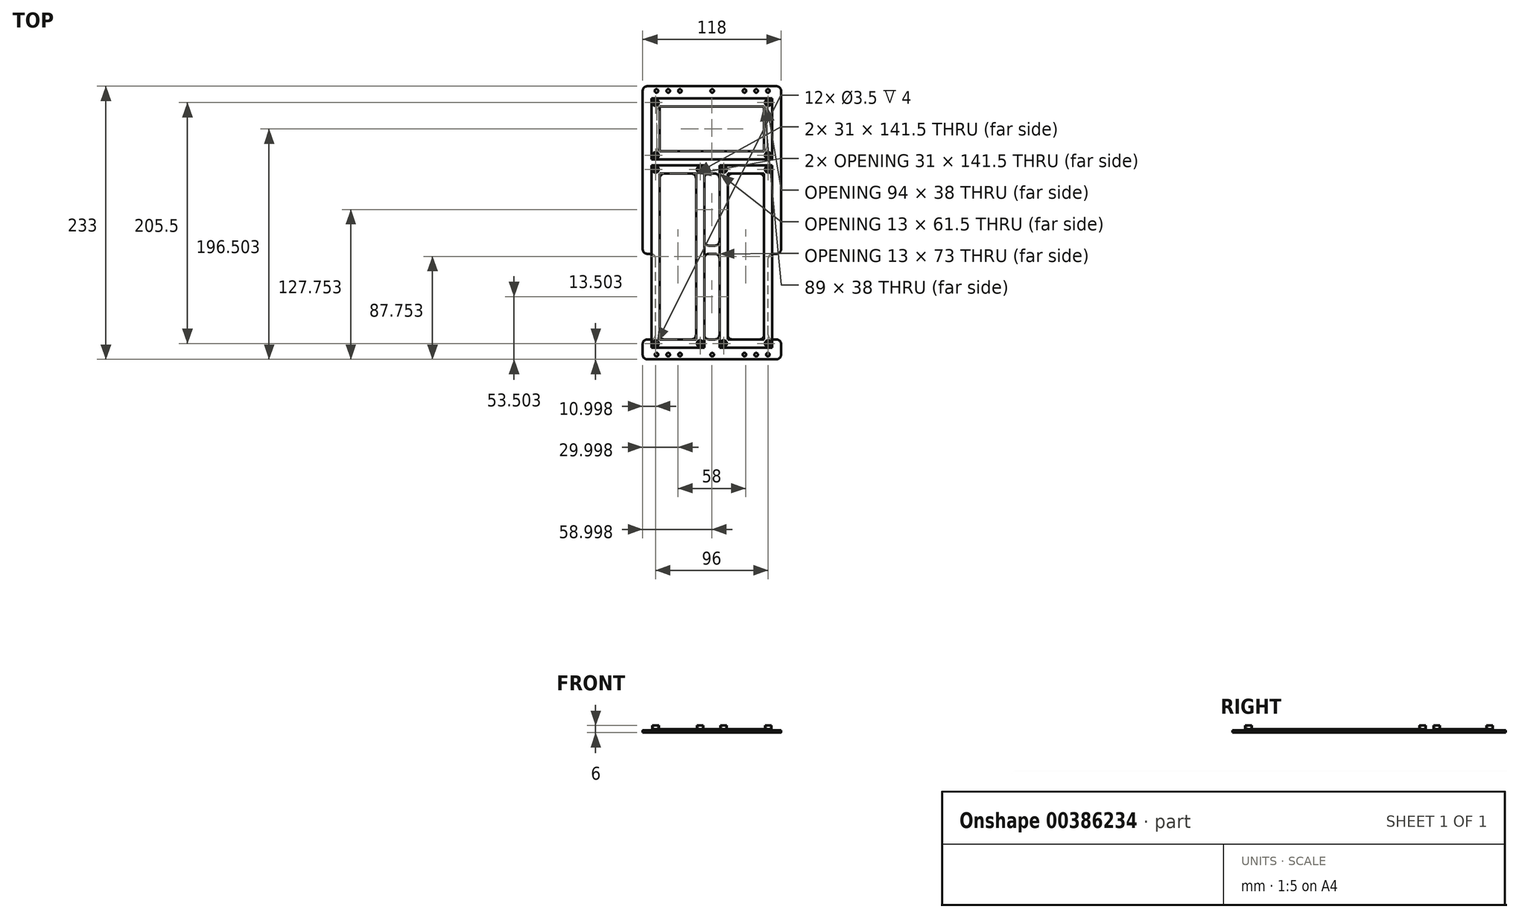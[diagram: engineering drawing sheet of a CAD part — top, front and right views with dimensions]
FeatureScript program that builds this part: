
annotation { "Feature Type Name" : "Feature", "Feature Type Description" : "" }
export const myFeature = defineFeature(function(context is Context, id is Id, definition is map)
    precondition{}
    {
        {
            var Q0;
            Q0=qCreatedBy(makeId("Top.planeOp"),FACE);
            var sketch = newSketch(context, id + "F0", { "sketchPlane" : qUnion([Q0])});
            skLineSegment(sketch, "E0.bottom", {"start": v(-51.8, 67.1) * mm, "end": v(51.2, 67.1) * mm});
            skLineSegment(sketch, "E0.top", {"start": v(-51.8, 15.1) * mm, "end": v(51.2, 15.1) * mm});
            skLineSegment(sketch, "E0.left", {"start": v(-51.8, 67.1) * mm, "end": v(-51.8, 15.1) * mm});
            skLineSegment(sketch, "E0.right", {"start": v(51.2, 67.1) * mm, "end": v(51.2, 15.1) * mm});
            skCircle(sketch, "E1", {"center": v(-48.3, 63.6) * mm, "radius": 1.75 * mm});
            skCircle(sketch, "E2", {"center": v(-48.3, 18.6) * mm, "radius": 1.75 * mm});
            skCircle(sketch, "E3", {"center": v(47.7, 18.6) * mm, "radius": 1.75 * mm});
            skCircle(sketch, "E4", {"center": v(47.7, 63.6) * mm, "radius": 1.75 * mm});
            skLineSegment(sketch, "E5.bottom", {"start": v(-44.8, 22.1) * mm, "end": v(44.2, 22.1) * mm});
            skLineSegment(sketch, "E5.top", {"start": v(-44.8, 60.1) * mm, "end": v(44.2, 60.1) * mm});
            skLineSegment(sketch, "E5.left", {"start": v(-44.8, 22.1) * mm, "end": v(-44.8, 60.1) * mm});
            skLineSegment(sketch, "E5.right", {"start": v(44.2, 22.1) * mm, "end": v(44.2, 60.1) * mm});
            skCircle(sketch, "E6", {"center": v(-48.3, 63.6) * mm, "radius": 2.75 * mm});
            skCircle(sketch, "E7", {"center": v(-48.3, 18.6) * mm, "radius": 2.75 * mm});
            skCircle(sketch, "E8", {"center": v(47.7, 18.6) * mm, "radius": 2.75 * mm});
            skCircle(sketch, "E9", {"center": v(47.7, 63.6) * mm, "radius": 2.75 * mm});
            skSolve(sketch);
        }
        {
            var Q0;
            Q0=makeQuery(id+"F0.imprint","IMPRINT",FACE,{"disambiguationData":[TD([[makeQuery(id+"F0.imprint","IMPRINT",EDGE,{"derivedFrom":sQuery(id+"F0.wireOp",EDGE,"E0.bottom")}),-1.0]])]});
            extrude(context, id + "F1", {"entities" : qUnion([Q0]), "depth" : 1 * mm});
        }
        {
            var Q0;
            Q0=makeQuery(id+"F0.imprint","IMPRINT",FACE,{"disambiguationData":[TD([[makeQuery(id+"F0.imprint","IMPRINT",EDGE,{"derivedFrom":sQuery(id+"F0.wireOp",EDGE,"E1")}),-1.0]])]});
            var Q1;
            Q1=makeQuery(id+"F0.imprint","IMPRINT",FACE,{"disambiguationData":[TD([[makeQuery(id+"F0.imprint","IMPRINT",EDGE,{"derivedFrom":sQuery(id+"F0.wireOp",EDGE,"E4")}),-1.0]])]});
            var Q2;
            Q2=makeQuery(id+"F0.imprint","IMPRINT",FACE,{"disambiguationData":[TD([[makeQuery(id+"F0.imprint","IMPRINT",EDGE,{"derivedFrom":sQuery(id+"F0.wireOp",EDGE,"E3")}),-1.0]])]});
            var Q3;
            Q3=makeQuery(id+"F0.imprint","IMPRINT",FACE,{"disambiguationData":[TD([[makeQuery(id+"F0.imprint","IMPRINT",EDGE,{"derivedFrom":sQuery(id+"F0.wireOp",EDGE,"E2")}),-1.0]])]});
            extrude(context, id + "F2", {"entities" : qUnion([Q0, Q1, Q2, Q3]), "operationType" : NewBodyOperationType.ADD, "depth" : 4 * mm});
        }
        {
            var Q0;
            Q0=qCreatedBy(makeId("Top.planeOp"),FACE);
            var sketch = newSketch(context, id + "F3", { "sketchPlane" : qUnion([Q0])});
            skLineSegment(sketch, "E10.bottom", {"start": v(-51.8, 10.1) * mm, "end": v(-6.8, 10.1) * mm});
            skLineSegment(sketch, "E10.top", {"start": v(-51.8, -145.4) * mm, "end": v(-6.8, -145.4) * mm});
            skLineSegment(sketch, "E10.left", {"start": v(-51.8, 10.1) * mm, "end": v(-51.8, -145.4) * mm});
            skLineSegment(sketch, "E10.right", {"start": v(-6.8, 10.1) * mm, "end": v(-6.8, -145.4) * mm});
            skCircle(sketch, "E11", {"center": v(-48.3, 6.6) * mm, "radius": 1.75 * mm});
            skCircle(sketch, "E12", {"center": v(-48.3, -141.9) * mm, "radius": 1.75 * mm});
            skCircle(sketch, "E13", {"center": v(-10.3, -141.9) * mm, "radius": 1.75 * mm});
            skCircle(sketch, "E14", {"center": v(-10.3, 6.6) * mm, "radius": 1.75 * mm});
            skLineSegment(sketch, "E15.bottom", {"start": v(-44.8, -138.4) * mm, "end": v(-13.8, -138.4) * mm});
            skLineSegment(sketch, "E15.top", {"start": v(-44.8, 3.1) * mm, "end": v(-13.8, 3.1) * mm});
            skLineSegment(sketch, "E15.left", {"start": v(-44.8, -138.4) * mm, "end": v(-44.8, 3.1) * mm});
            skLineSegment(sketch, "E15.right", {"start": v(-13.8, -138.4) * mm, "end": v(-13.8, 3.1) * mm});
            skCircle(sketch, "E16", {"center": v(-48.3, 6.6) * mm, "radius": 2.75 * mm});
            skCircle(sketch, "E17", {"center": v(-48.3, -141.9) * mm, "radius": 2.75 * mm});
            skCircle(sketch, "E18", {"center": v(-10.3, -141.9) * mm, "radius": 2.75 * mm});
            skCircle(sketch, "E19", {"center": v(-10.3, 6.6) * mm, "radius": 2.75 * mm});
            skSolve(sketch);
        }
        {
            var Q0;
            Q0=qCreatedBy(makeId("Top.planeOp"),FACE);
            var sketch = newSketch(context, id + "F4", { "sketchPlane" : qUnion([Q0])});
            skLineSegment(sketch, "E20.bottom", {"start": v(6.2, 10.1) * mm, "end": v(51.2, 10.1) * mm});
            skLineSegment(sketch, "E20.top", {"start": v(6.2, -145.4) * mm, "end": v(51.2, -145.4) * mm});
            skLineSegment(sketch, "E20.left", {"start": v(6.2, 10.1) * mm, "end": v(6.2, -145.4) * mm});
            skLineSegment(sketch, "E20.right", {"start": v(51.2, 10.1) * mm, "end": v(51.2, -145.4) * mm});
            skCircle(sketch, "E21", {"center": v(9.7, 6.6) * mm, "radius": 1.75 * mm});
            skCircle(sketch, "E22", {"center": v(9.7, -141.9) * mm, "radius": 1.75 * mm});
            skCircle(sketch, "E23", {"center": v(47.7, -141.9) * mm, "radius": 1.75 * mm});
            skCircle(sketch, "E24", {"center": v(47.7, 6.6) * mm, "radius": 1.75 * mm});
            skLineSegment(sketch, "E25.bottom", {"start": v(13.2, -138.4) * mm, "end": v(44.2, -138.4) * mm});
            skLineSegment(sketch, "E25.top", {"start": v(13.2, 3.1) * mm, "end": v(44.2, 3.1) * mm});
            skLineSegment(sketch, "E25.left", {"start": v(13.2, -138.4) * mm, "end": v(13.2, 3.1) * mm});
            skLineSegment(sketch, "E25.right", {"start": v(44.2, -138.4) * mm, "end": v(44.2, 3.1) * mm});
            skCircle(sketch, "E26", {"center": v(9.7, 6.6) * mm, "radius": 2.75 * mm});
            skCircle(sketch, "E27", {"center": v(9.7, -141.9) * mm, "radius": 2.75 * mm});
            skCircle(sketch, "E28", {"center": v(47.7, -141.9) * mm, "radius": 2.75 * mm});
            skCircle(sketch, "E29", {"center": v(47.7, 6.6) * mm, "radius": 2.75 * mm});
            skSolve(sketch);
        }
        {
            var Q0;
            Q0=makeQuery(id+"F3.imprint","IMPRINT",FACE,{"disambiguationData":[TD([[makeQuery(id+"F3.imprint","IMPRINT",EDGE,{"derivedFrom":sQuery(id+"F3.wireOp",EDGE,"E10.bottom")}),-1.0]])]});
            var Q1;
            Q1=makeQuery(id+"F4.imprint","IMPRINT",FACE,{"disambiguationData":[TD([[makeQuery(id+"F4.imprint","IMPRINT",EDGE,{"derivedFrom":sQuery(id+"F4.wireOp",EDGE,"E20.bottom")}),-1.0]])]});
            extrude(context, id + "F5", {"entities" : qUnion([Q0, Q1]), "depth" : 1 * mm});
        }
        {
            var Q0;
            Q0=makeQuery(id+"F3.imprint","IMPRINT",FACE,{"disambiguationData":[TD([[makeQuery(id+"F3.imprint","IMPRINT",EDGE,{"derivedFrom":sQuery(id+"F3.wireOp",EDGE,"E12")}),-1.0]])]});
            var Q1;
            Q1=makeQuery(id+"F3.imprint","IMPRINT",FACE,{"disambiguationData":[TD([[makeQuery(id+"F3.imprint","IMPRINT",EDGE,{"derivedFrom":sQuery(id+"F3.wireOp",EDGE,"E13")}),-1.0]])]});
            var Q2;
            Q2=makeQuery(id+"F3.imprint","IMPRINT",FACE,{"disambiguationData":[TD([[makeQuery(id+"F3.imprint","IMPRINT",EDGE,{"derivedFrom":sQuery(id+"F3.wireOp",EDGE,"E11")}),-1.0]])]});
            var Q3;
            Q3=makeQuery(id+"F3.imprint","IMPRINT",FACE,{"disambiguationData":[TD([[makeQuery(id+"F3.imprint","IMPRINT",EDGE,{"derivedFrom":sQuery(id+"F3.wireOp",EDGE,"E14")}),-1.0]])]});
            var Q4;
            Q4=makeQuery(id+"F4.imprint","IMPRINT",FACE,{"disambiguationData":[TD([[makeQuery(id+"F4.imprint","IMPRINT",EDGE,{"derivedFrom":sQuery(id+"F4.wireOp",EDGE,"E21")}),-1.0]])]});
            var Q5;
            Q5=makeQuery(id+"F4.imprint","IMPRINT",FACE,{"disambiguationData":[TD([[makeQuery(id+"F4.imprint","IMPRINT",EDGE,{"derivedFrom":sQuery(id+"F4.wireOp",EDGE,"E24")}),-1.0]])]});
            var Q6;
            Q6=makeQuery(id+"F4.imprint","IMPRINT",FACE,{"disambiguationData":[TD([[makeQuery(id+"F4.imprint","IMPRINT",EDGE,{"derivedFrom":sQuery(id+"F4.wireOp",EDGE,"E22")}),-1.0]])]});
            var Q7;
            Q7=makeQuery(id+"F4.imprint","IMPRINT",FACE,{"disambiguationData":[TD([[makeQuery(id+"F4.imprint","IMPRINT",EDGE,{"derivedFrom":sQuery(id+"F4.wireOp",EDGE,"E23")}),-1.0]])]});
            extrude(context, id + "F6", {"entities" : qUnion([Q0, Q1, Q2, Q3, Q4, Q5, Q6, Q7]), "operationType" : NewBodyOperationType.ADD, "depth" : 4 * mm});
        }
        {
            var Q0;
            Q0=qCreatedBy(makeId("Top.planeOp"),FACE);
            var sketch = newSketch(context, id + "F7", { "sketchPlane" : qUnion([Q0])});
            skLineSegment(sketch, "E30.bottom", {"start": v(58.7, 77.6) * mm, "end": v(-59.3, 77.6) * mm});
            skLineSegment(sketch, "E30.top", {"start": v(58.7, -155.4) * mm, "end": v(-59.3, -155.4) * mm});
            skLineSegment(sketch, "E30.left", {"start": v(58.7, 77.6) * mm, "end": v(58.7, -155.4) * mm});
            skLineSegment(sketch, "E30.right", {"start": v(-59.3, 77.6) * mm, "end": v(-59.3, -155.4) * mm});
            skPoint(sketch, "E30.middle", {"position": v(-0.3, -38.9) * mm});
            skPoint(sketch, "E31", {"position": v(-51.8, 27.1) * mm});
            skPoint(sketch, "E32", {"position": v(-51.8, 57.1) * mm});
            skLineSegment(sketch, "E33.bottom", {"start": v(-47.3, 60.1) * mm, "end": v(46.7, 60.1) * mm});
            skLineSegment(sketch, "E33.top", {"start": v(-47.3, 22.1) * mm, "end": v(46.7, 22.1) * mm});
            skLineSegment(sketch, "E33.left", {"start": v(-47.3, 60.1) * mm, "end": v(-47.3, 22.1) * mm});
            skLineSegment(sketch, "E33.right", {"start": v(46.7, 60.1) * mm, "end": v(46.7, 22.1) * mm});
            skLineSegment(sketch, "E34.bottom", {"start": v(13.2, -138.4) * mm, "end": v(44.2, -138.4) * mm});
            skLineSegment(sketch, "E34.top", {"start": v(13.2, 3.1) * mm, "end": v(44.2, 3.1) * mm});
            skLineSegment(sketch, "E34.left", {"start": v(13.2, -138.4) * mm, "end": v(13.2, 3.1) * mm});
            skLineSegment(sketch, "E34.right", {"start": v(44.2, -138.4) * mm, "end": v(44.2, 3.1) * mm});
            skLineSegment(sketch, "E35.bottom", {"start": v(-44.8, -138.4) * mm, "end": v(-13.8, -138.4) * mm});
            skLineSegment(sketch, "E35.top", {"start": v(-44.8, 3.1) * mm, "end": v(-13.8, 3.1) * mm});
            skLineSegment(sketch, "E35.left", {"start": v(-44.8, -138.4) * mm, "end": v(-44.8, 3.1) * mm});
            skLineSegment(sketch, "E35.right", {"start": v(-13.8, -138.4) * mm, "end": v(-13.8, 3.1) * mm});
            skLineSegment(sketch, "E36.bottom", {"start": v(-6.8, -138.4) * mm, "end": v(6.2, -138.4) * mm});
            skLineSegment(sketch, "E36.top", {"start": v(-6.8, -65.4) * mm, "end": v(6.2, -65.4) * mm});
            skLineSegment(sketch, "E36.left", {"start": v(-6.8, -138.4) * mm, "end": v(-6.8, -65.4) * mm});
            skLineSegment(sketch, "E36.right", {"start": v(6.2, -138.4) * mm, "end": v(6.2, -65.4) * mm});
            skLineSegment(sketch, "E37.bottom", {"start": v(-6.8, 3.1) * mm, "end": v(6.2, 3.1) * mm});
            skLineSegment(sketch, "E37.top", {"start": v(-6.8, -58.4) * mm, "end": v(6.2, -58.4) * mm});
            skLineSegment(sketch, "E37.left", {"start": v(-6.8, 3.1) * mm, "end": v(-6.8, -58.4) * mm});
            skLineSegment(sketch, "E37.right", {"start": v(6.2, 3.1) * mm, "end": v(6.2, -58.4) * mm});
            skLineSegment(sketch, "E38.bottom", {"start": v(-59.3, -138.4) * mm, "end": v(-48.3, -138.4) * mm});
            skLineSegment(sketch, "E38.top", {"start": v(-59.3, -65.4) * mm, "end": v(-48.3, -65.4) * mm});
            skLineSegment(sketch, "E38.left", {"start": v(-59.3, -138.4) * mm, "end": v(-59.3, -65.4) * mm});
            skLineSegment(sketch, "E38.right", {"start": v(-48.3, -138.4) * mm, "end": v(-48.3, -65.4) * mm});
            skLineSegment(sketch, "E39.bottom", {"start": v(47.7, -138.4) * mm, "end": v(58.7, -138.4) * mm});
            skLineSegment(sketch, "E39.top", {"start": v(47.7, -65.4) * mm, "end": v(58.7, -65.4) * mm});
            skLineSegment(sketch, "E39.left", {"start": v(47.7, -138.4) * mm, "end": v(47.7, -65.4) * mm});
            skLineSegment(sketch, "E39.right", {"start": v(58.7, -138.4) * mm, "end": v(58.7, -65.4) * mm});
            skCircle(sketch, "E40", {"center": v(0, -151.4) * mm, "radius": 1.5 * mm});
            skCircle(sketch, "E41", {"center": v(-37.5, -151.4) * mm, "radius": 1.5 * mm});
            skCircle(sketch, "E42", {"center": v(37.5, -151.4) * mm, "radius": 1.5 * mm});
            skCircle(sketch, "E43", {"center": v(0, 73.6) * mm, "radius": 1.5 * mm});
            skCircle(sketch, "E44", {"center": v(37.5, 73.6) * mm, "radius": 1.5 * mm});
            skCircle(sketch, "E45", {"center": v(-37.5, 73.6) * mm, "radius": 1.5 * mm});
            skCircle(sketch, "E46", {"center": v(-27.5, -151.4) * mm, "radius": 1.5 * mm});
            skCircle(sketch, "E47", {"center": v(-47.5, -151.4) * mm, "radius": 1.5 * mm});
            skCircle(sketch, "E48", {"center": v(27.5, -151.4) * mm, "radius": 1.5 * mm});
            skCircle(sketch, "E49", {"center": v(47.5, -151.4) * mm, "radius": 1.5 * mm});
            skCircle(sketch, "E50", {"center": v(-47.5, 73.6) * mm, "radius": 1.5 * mm});
            skCircle(sketch, "E51", {"center": v(-27.5, 73.6) * mm, "radius": 1.5 * mm});
            skCircle(sketch, "E52", {"center": v(27.5, 73.6) * mm, "radius": 1.5 * mm});
            skCircle(sketch, "E53", {"center": v(47.5, 73.6) * mm, "radius": 1.5 * mm});
            skCircle(sketch, "E54", {"center": v(-48.3, -141.9) * mm, "radius": 1.25 * mm});
            skCircle(sketch, "E55", {"center": v(-10.3, -141.9) * mm, "radius": 1.25 * mm});
            skCircle(sketch, "E56", {"center": v(9.7, -141.9) * mm, "radius": 1.25 * mm});
            skCircle(sketch, "E57", {"center": v(47.7, -141.9) * mm, "radius": 1.25 * mm});
            skCircle(sketch, "E58", {"center": v(47.7, 6.6) * mm, "radius": 1.25 * mm});
            skCircle(sketch, "E59", {"center": v(9.7, 6.6) * mm, "radius": 1.25 * mm});
            skCircle(sketch, "E60", {"center": v(-10.3, 6.6) * mm, "radius": 1.25 * mm});
            skCircle(sketch, "E61", {"center": v(-48.3, 6.6) * mm, "radius": 1.25 * mm});
            skCircle(sketch, "E62", {"center": v(-48.3, 18.6) * mm, "radius": 1.25 * mm});
            skCircle(sketch, "E63", {"center": v(-48.3, 63.6) * mm, "radius": 1.25 * mm});
            skCircle(sketch, "E64", {"center": v(47.7, 63.6) * mm, "radius": 1.25 * mm});
            skCircle(sketch, "E65", {"center": v(47.7, 18.6) * mm, "radius": 1.25 * mm});
            skSolve(sketch);
        }
        {
            var Q0;
            Q0=makeQuery(id+"F7.imprint","IMPRINT",FACE,{"disambiguationData":[TD([[makeQuery(id+"F7.imprint","IMPRINT",EDGE,{"derivedFrom":sQuery(id+"F7.wireOp",EDGE,"E30.bottom")}),1.0]])]});
            var Q1;
            {var subQ0=sQuery(id+"F7.wireOp",EDGE,"EuvkgEiH-Gyot-M5OE-X1c4-2lYT4B40r9jS");Q1=makeQuery(id+"F7.imprint","IMPRINT",FACE,{"disambiguationData":[TD([[makeQuery(id+"F7.imprint","IMPRINT",EDGE,{"derivedFrom":subQ0}),1.0]])]});}
            var Q2;
            {var subQ0=sQuery(id+"F7.wireOp",EDGE,"UMoBTgPs-a6LY-YM4x-fqEf-t7va54NRuSjA");Q2=makeQuery(id+"F7.imprint","IMPRINT",FACE,{"disambiguationData":[TD([[makeQuery(id+"F7.imprint","IMPRINT",EDGE,{"derivedFrom":subQ0}),1.0]])]});}
            extrude(context, id + "F8", {"entities" : qUnion([Q0, Q1, Q2]), "oppositeDirection" : true, "depth" : 2 * mm});
        }
        {
            var Q0;
            Q0=makeQuery(id+"F8.opExtrude","SWEPT_EDGE",EDGE,{"disambiguationData":[OSD([sQuery(id+"F7.wireOp",EDGE,"E33.top"),sQuery(id+"F7.wireOp",EDGE,"E33.right")])]});
            var Q1;
            Q1=makeQuery(id+"F8.opExtrude","SWEPT_EDGE",EDGE,{"disambiguationData":[OSD([sQuery(id+"F7.wireOp",EDGE,"E30.bottom"),sQuery(id+"F7.wireOp",EDGE,"E30.right")])]});
            var Q2;
            Q2=makeQuery(id+"F8.opExtrude","SWEPT_EDGE",EDGE,{"disambiguationData":[OSD([sQuery(id+"F7.wireOp",EDGE,"E30.top"),sQuery(id+"F7.wireOp",EDGE,"E30.right")])]});
            var Q3;
            Q3=makeQuery(id+"F8.opExtrude","SWEPT_EDGE",EDGE,{"disambiguationData":[OSD([sQuery(id+"F7.wireOp",EDGE,"E30.bottom"),sQuery(id+"F7.wireOp",EDGE,"E30.left")])]});
            var Q4;
            Q4=makeQuery(id+"F8.opExtrude","SWEPT_EDGE",EDGE,{"disambiguationData":[OSD([sQuery(id+"F7.wireOp",EDGE,"E34.bottom"),sQuery(id+"F7.wireOp",EDGE,"E34.right")])]});
            var Q5;
            Q5=makeQuery(id+"F8.opExtrude","SWEPT_EDGE",EDGE,{"disambiguationData":[OSD([sQuery(id+"F7.wireOp",EDGE,"E35.bottom"),sQuery(id+"F7.wireOp",EDGE,"E35.right")])]});
            var Q6;
            Q6=makeQuery(id+"F8.opExtrude","SWEPT_EDGE",EDGE,{"disambiguationData":[OSD([sQuery(id+"F7.wireOp",EDGE,"E35.bottom"),sQuery(id+"F7.wireOp",EDGE,"E35.left")])]});
            var Q7;
            Q7=makeQuery(id+"F8.opExtrude","SWEPT_EDGE",EDGE,{"disambiguationData":[OSD([sQuery(id+"F7.wireOp",EDGE,"E34.bottom"),sQuery(id+"F7.wireOp",EDGE,"E34.left")])]});
            var Q8;
            Q8=makeQuery(id+"F8.opExtrude","SWEPT_EDGE",EDGE,{"disambiguationData":[OSD([sQuery(id+"F7.wireOp",EDGE,"E33.top"),sQuery(id+"F7.wireOp",EDGE,"E33.left")])]});
            var Q9;
            Q9=makeQuery(id+"F8.opExtrude","SWEPT_EDGE",EDGE,{"disambiguationData":[OSD([sQuery(id+"F7.wireOp",EDGE,"E30.top"),sQuery(id+"F7.wireOp",EDGE,"E30.left")])]});
            var Q10;
            Q10=makeQuery(id+"F8.opExtrude","SWEPT_EDGE",EDGE,{"disambiguationData":[OSD([sQuery(id+"F7.wireOp",EDGE,"E35.top"),sQuery(id+"F7.wireOp",EDGE,"E35.left")])]});
            var Q11;
            Q11=makeQuery(id+"F8.opExtrude","SWEPT_EDGE",EDGE,{"disambiguationData":[OSD([sQuery(id+"F7.wireOp",EDGE,"E33.bottom"),sQuery(id+"F7.wireOp",EDGE,"E33.left")])]});
            var Q12;
            Q12=makeQuery(id+"F8.opExtrude","SWEPT_EDGE",EDGE,{"disambiguationData":[OSD([sQuery(id+"F7.wireOp",EDGE,"E34.top"),sQuery(id+"F7.wireOp",EDGE,"E34.left")])]});
            var Q13;
            Q13=makeQuery(id+"F8.opExtrude","SWEPT_EDGE",EDGE,{"disambiguationData":[OSD([sQuery(id+"F7.wireOp",EDGE,"E33.bottom"),sQuery(id+"F7.wireOp",EDGE,"E33.right")])]});
            var Q14;
            Q14=makeQuery(id+"F8.opExtrude","SWEPT_EDGE",EDGE,{"disambiguationData":[OSD([sQuery(id+"F7.wireOp",EDGE,"E34.top"),sQuery(id+"F7.wireOp",EDGE,"E34.right")])]});
            var Q15;
            Q15=makeQuery(id+"F8.opExtrude","SWEPT_EDGE",EDGE,{"disambiguationData":[OSD([sQuery(id+"F7.wireOp",EDGE,"E35.top"),sQuery(id+"F7.wireOp",EDGE,"E35.right")])]});
            var Q16;
            Q16=makeQuery(id+"F8.opExtrude","SWEPT_EDGE",EDGE,{"disambiguationData":[OSD([sQuery(id+"F7.wireOp",EDGE,"E36.top"),sQuery(id+"F7.wireOp",EDGE,"E36.left")])]});
            var Q17;
            Q17=makeQuery(id+"F8.opExtrude","SWEPT_EDGE",EDGE,{"disambiguationData":[OSD([sQuery(id+"F7.wireOp",EDGE,"E37.bottom"),sQuery(id+"F7.wireOp",EDGE,"E37.left")])]});
            var Q18;
            Q18=makeQuery(id+"F8.opExtrude","SWEPT_EDGE",EDGE,{"disambiguationData":[OSD([sQuery(id+"F7.wireOp",EDGE,"E37.bottom"),sQuery(id+"F7.wireOp",EDGE,"E37.right")])]});
            var Q19;
            Q19=makeQuery(id+"F8.opExtrude","SWEPT_EDGE",EDGE,{"disambiguationData":[OSD([sQuery(id+"F7.wireOp",EDGE,"E36.top"),sQuery(id+"F7.wireOp",EDGE,"E36.right")])]});
            var Q20;
            Q20=makeQuery(id+"F8.opExtrude","SWEPT_EDGE",EDGE,{"disambiguationData":[OSD([sQuery(id+"F7.wireOp",EDGE,"E37.top"),sQuery(id+"F7.wireOp",EDGE,"E37.right")])]});
            var Q21;
            Q21=makeQuery(id+"F8.opExtrude","SWEPT_EDGE",EDGE,{"disambiguationData":[OSD([sQuery(id+"F7.wireOp",EDGE,"E36.bottom"),sQuery(id+"F7.wireOp",EDGE,"E36.right")])]});
            var Q22;
            Q22=makeQuery(id+"F8.opExtrude","SWEPT_EDGE",EDGE,{"disambiguationData":[OSD([sQuery(id+"F7.wireOp",EDGE,"E37.top"),sQuery(id+"F7.wireOp",EDGE,"E37.left")])]});
            var Q23;
            Q23=makeQuery(id+"F8.opExtrude","SWEPT_EDGE",EDGE,{"disambiguationData":[OSD([sQuery(id+"F7.wireOp",EDGE,"E36.bottom"),sQuery(id+"F7.wireOp",EDGE,"E36.left")])]});
            var Q24;
            Q24=makeQuery(id+"F8.opExtrude","SWEPT_EDGE",EDGE,{"disambiguationData":[OSD([sQuery(id+"F7.wireOp",EDGE,"E38.bottom"),sQuery(id+"F7.wireOp",EDGE,"E38.right")])]});
            var Q25;
            Q25=makeQuery(id+"F8.opExtrude","SWEPT_EDGE",EDGE,{"disambiguationData":[OSD([sQuery(id+"F7.wireOp",EDGE,"E30.right"),sQuery(id+"F7.wireOp",EDGE,"E38.bottom"),sQuery(id+"F7.wireOp",EDGE,"E38.left")])]});
            var Q26;
            Q26=makeQuery(id+"F8.opExtrude","SWEPT_EDGE",EDGE,{"disambiguationData":[OSD([sQuery(id+"F7.wireOp",EDGE,"E30.right"),sQuery(id+"F7.wireOp",EDGE,"E38.top"),sQuery(id+"F7.wireOp",EDGE,"E38.left")])]});
            var Q27;
            Q27=makeQuery(id+"F8.opExtrude","SWEPT_EDGE",EDGE,{"disambiguationData":[OSD([sQuery(id+"F7.wireOp",EDGE,"E30.left"),sQuery(id+"F7.wireOp",EDGE,"E39.bottom"),sQuery(id+"F7.wireOp",EDGE,"E39.right")])]});
            var Q28;
            Q28=makeQuery(id+"F8.opExtrude","SWEPT_EDGE",EDGE,{"disambiguationData":[OSD([sQuery(id+"F7.wireOp",EDGE,"E39.bottom"),sQuery(id+"F7.wireOp",EDGE,"E39.left")])]});
            var Q29;
            Q29=makeQuery(id+"F8.opExtrude","SWEPT_EDGE",EDGE,{"disambiguationData":[OSD([sQuery(id+"F7.wireOp",EDGE,"E30.left"),sQuery(id+"F7.wireOp",EDGE,"E39.top"),sQuery(id+"F7.wireOp",EDGE,"E39.right")])]});
            var Q30;
            Q30=makeQuery(id+"F8.opExtrude","SWEPT_EDGE",EDGE,{"disambiguationData":[OSD([sQuery(id+"F7.wireOp",EDGE,"E39.top"),sQuery(id+"F7.wireOp",EDGE,"E39.left")])]});
            var Q31;
            Q31=makeQuery(id+"F8.opExtrude","SWEPT_EDGE",EDGE,{"disambiguationData":[OSD([sQuery(id+"F7.wireOp",EDGE,"E38.top"),sQuery(id+"F7.wireOp",EDGE,"E38.right")])]});
            fillet(context, id + "F9", {"entities" : qUnion([Q0, Q1, Q2, Q3, Q4, Q5, Q6, Q7, Q8, Q9, Q10, Q11, Q12, Q13, Q14, Q15, Q16, Q17, Q18, Q19, Q20, Q21, Q22, Q23, Q24, Q25, Q26, Q27, Q28, Q29, Q30, Q31]), "radius" : 4 * mm, "tangentPropagation" : true, "allowEdgeOverflow" : false});
        }
    });
